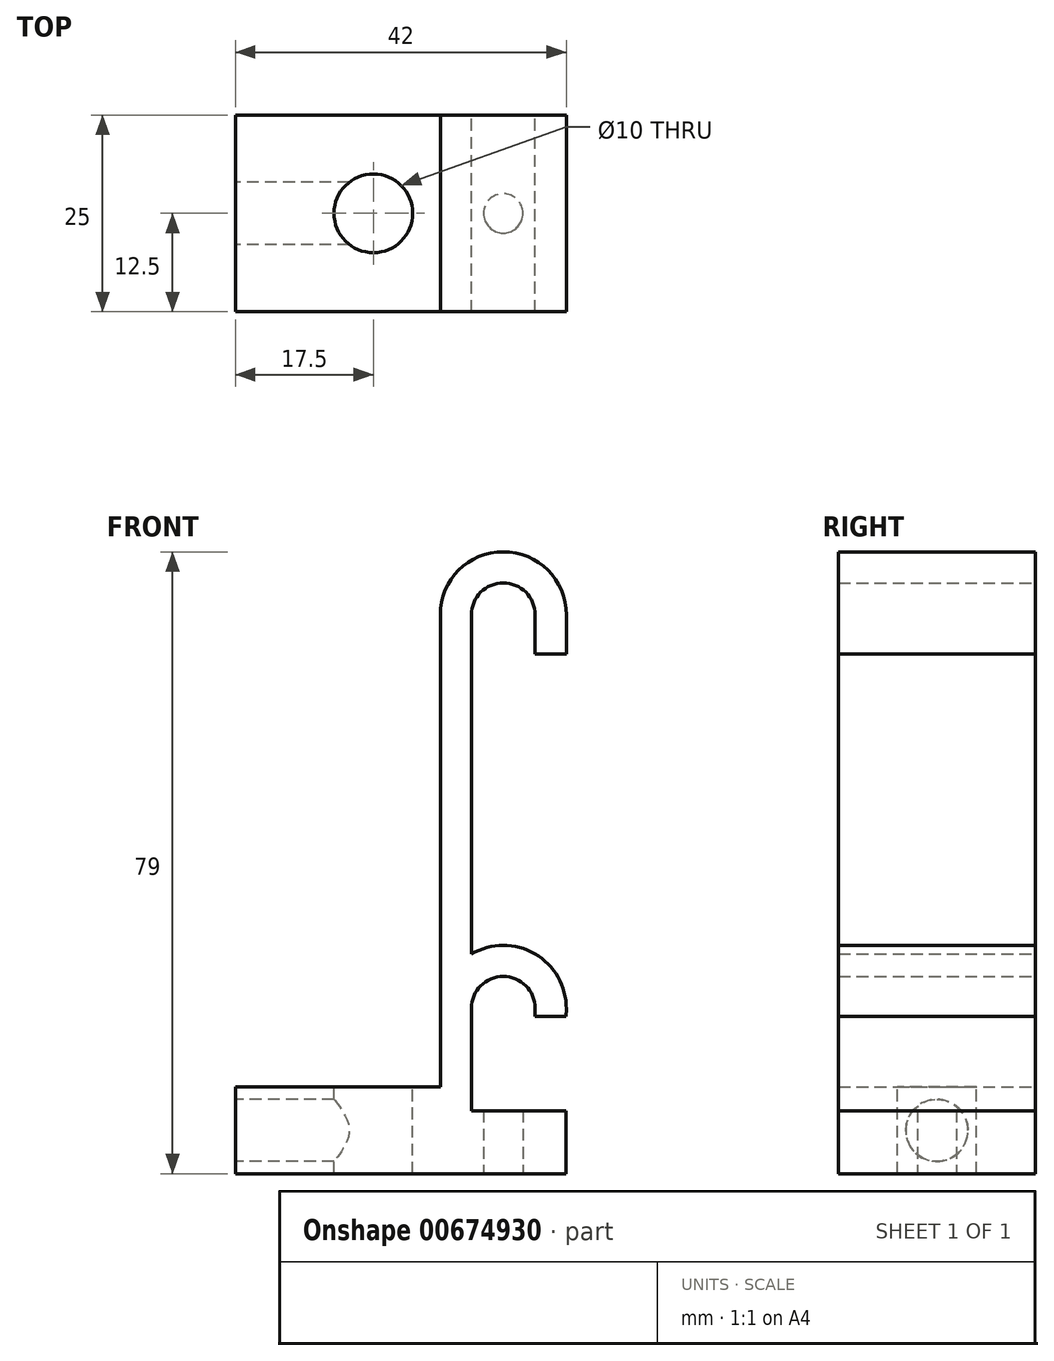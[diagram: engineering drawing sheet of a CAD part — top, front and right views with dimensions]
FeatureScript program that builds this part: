
annotation { "Feature Type Name" : "Feature", "Feature Type Description" : "" }
export const myFeature = defineFeature(function(context is Context, id is Id, definition is map)
    precondition{}
    {
        {
            var Q0;
            Q0=qCreatedBy(makeId("Front.planeOp"),FACE);
            var sketch = newSketch(context, id + "F0", { "sketchPlane" : qUnion([Q0])});
            skArc(sketch, "E0", {"start": v(4.05, 0) * mm, "mid": v(0, 4.05) * mm, "end": v(-4.05, 0) * mm});
            skArc(sketch, "E1", {"start": v(4.05, -50) * mm, "mid": v(0, -45.95) * mm, "end": v(-4.05, -50) * mm});
            skLineSegment(sketch, "E2", {"start": v(4.05, 0) * mm, "end": v(4.05, -5) * mm});
            skLineSegment(sketch, "E3", {"start": v(4.05, -5) * mm, "end": v(8, -5) * mm});
            skArc(sketch, "E4", {"start": v(8, 0) * mm, "mid": v(0, 8) * mm, "end": v(-8, 0) * mm});
            skArc(sketch, "E5", {"start": v(8, -50.07) * mm, "mid": v(4, -43.08) * mm, "end": v(-4.05, -43.1) * mm});
            skLineSegment(sketch, "E6", {"start": v(8, 0) * mm, "end": v(8, -5) * mm});
            skLineSegment(sketch, "E7", {"start": v(-4.05, 0) * mm, "end": v(-4.05, -43.1) * mm});
            skLineSegment(sketch, "E8", {"start": v(-8, 0) * mm, "end": v(-8, -50) * mm});
            skLineSegment(sketch, "E9", {"start": v(4.05, -50) * mm, "end": v(4.05, -51) * mm});
            skLineSegment(sketch, "E10", {"start": v(4.05, -51) * mm, "end": v(8, -51) * mm});
            skLineSegment(sketch, "E11", {"start": v(8, -51) * mm, "end": v(8, -50) * mm});
            skLineSegment(sketch, "E12", {"start": v(-8, -50) * mm, "end": v(-8, -60) * mm});
            skLineSegment(sketch, "E13", {"start": v(-8, -60) * mm, "end": v(-34, -60) * mm});
            skLineSegment(sketch, "E14", {"start": v(-34, -60) * mm, "end": v(-34, -71) * mm});
            skLineSegment(sketch, "E15", {"start": v(-34, -71) * mm, "end": v(-4.05, -71) * mm});
            skLineSegment(sketch, "E16", {"start": v(-4.05, -71) * mm, "end": v(-4.34, -70.54) * mm});
            skLineSegment(sketch, "E17", {"start": v(-4.05, -63) * mm, "end": v(-4.05, -50) * mm});
            skLineSegment(sketch, "E18.bottom", {"start": v(-4.05, -71) * mm, "end": v(8, -71) * mm});
            skLineSegment(sketch, "E18.top", {"start": v(-4.05, -63) * mm, "end": v(8, -63) * mm});
            skLineSegment(sketch, "E18.right", {"start": v(8, -71) * mm, "end": v(8, -63) * mm});
            skSolve(sketch);
        }
        {
            var Q0;
            Q0=makeQuery(id+"F0.imprint","IMPRINT",FACE,{"disambiguationData":[TD([[makeQuery(id+"F0.imprint","IMPRINT",EDGE,{"derivedFrom":sQuery(id+"F0.wireOp",EDGE,"E0")}),-1.0]])]});
            var Q1;
            Q1=makeQuery(id+"F0.imprint","IMPRINT",FACE,{"disambiguationData":[TD([[makeQuery(id+"F0.imprint","IMPRINT",EDGE,{"derivedFrom":sQuery(id+"F0.wireOp",EDGE,"E18.bottom")}),1.0]])]});
            extrude(context, id + "F1", {"entities" : qUnion([Q0, Q1]), "depth" : 25 * mm, "offsetDistance" : 25 * mm});
        }
        {
            var Q0;
            Q0=makeQuery(id+"F1.opExtrude","SWEPT_FACE",FACE,{"disambiguationData":[OSD([sQuery(id+"F0.wireOp",EDGE,"E13")])]});
            var sketch = newSketch(context, id + "F2", { "sketchPlane" : qUnion([Q0])});
            skCircle(sketch, "E19", {"center": v(-16.5, -12.5) * mm, "radius": 5 * mm});
            skLineSegment(sketch, "E20", {"start": v(-16.5, -12.5) * mm, "end": v(-16.5, -32.12) * mm, "construction": true});
            skLineSegment(sketch, "E21", {"start": v(-16.5, -12.5) * mm, "end": v(-33.19, -12.5) * mm, "construction": true});
            skSolve(sketch);
        }
        {
            var Q0;
            Q0=makeQuery(id+"F2.imprint","IMPRINT",FACE,{"disambiguationData":[TD([[makeQuery(id+"F2.imprint","IMPRINT",EDGE,{"derivedFrom":sQuery(id+"F2.wireOp",EDGE,"E19")}),1.0]])]});
            extrude(context, id + "F3", {"entities" : qUnion([Q0]), "operationType" : NewBodyOperationType.REMOVE, "oppositeDirection" : true, "depth" : 25 * mm, "offsetDistance" : 25 * mm});
        }
        {
            var Q0;
            Q0=makeQuery(id+"F1.opExtrude","SWEPT_FACE",FACE,{"disambiguationData":[OSD([sQuery(id+"F0.wireOp",EDGE,"E15"),sQuery(id+"F0.wireOp",EDGE,"E18.bottom")])]});
            var sketch = newSketch(context, id + "F4", { "sketchPlane" : qUnion([Q0])});
            skCircle(sketch, "E22", {"center": v(0, 12.5) * mm, "radius": 2.5 * mm});
            skPoint(sketch, "E22.centerSnap0", {"position": v(8, 12.5) * mm});
            skSolve(sketch);
        }
        {
            var Q0;
            Q0=makeQuery(id+"F4.imprint","IMPRINT",FACE,{"disambiguationData":[TD([[makeQuery(id+"F4.imprint","IMPRINT",EDGE,{"derivedFrom":sQuery(id+"F4.wireOp",EDGE,"E22")}),1.0]])]});
            extrude(context, id + "F5", {"entities" : qUnion([Q0]), "operationType" : NewBodyOperationType.REMOVE, "oppositeDirection" : true, "depth" : 15 * mm, "offsetDistance" : 25 * mm});
        }
        {
            var Q0;
            Q0=makeQuery(id+"F1.opExtrude","SWEPT_FACE",FACE,{"disambiguationData":[OSD([sQuery(id+"F0.wireOp",EDGE,"E14")])]});
            var sketch = newSketch(context, id + "F6", { "sketchPlane" : qUnion([Q0])});
            skLineSegment(sketch, "E23", {"start": v(0, -71) * mm, "end": v(25, -60) * mm, "construction": true});
            skLineSegment(sketch, "E24", {"start": v(0, -60) * mm, "end": v(25, -71) * mm, "construction": true});
            skCircle(sketch, "E25", {"center": v(12.5, -65.5) * mm, "radius": 3.95 * mm});
            skSolve(sketch);
        }
        {
            var Q0;
            Q0 = qSketchRegion(id + "F6", true);
            extrude(context, id + "F7", {"entities" : qUnion([Q0]), "operationType" : NewBodyOperationType.REMOVE, "oppositeDirection" : true, "depth" : 17 * mm, "offsetDistance" : 25 * mm});
        }
    });
